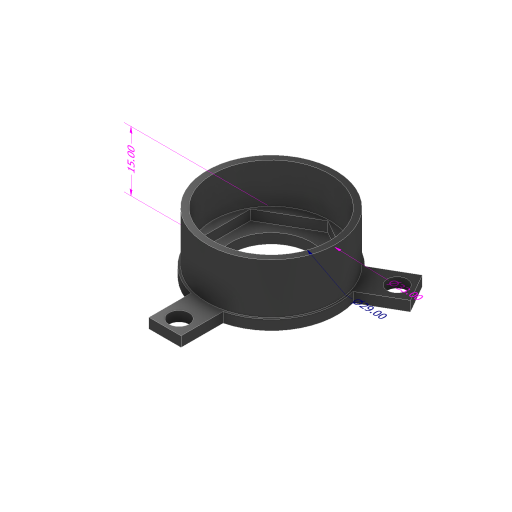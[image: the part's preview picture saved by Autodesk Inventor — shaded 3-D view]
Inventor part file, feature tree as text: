
AUTODESK INVENTOR PART (.ipt)
format: ipt  version: 2024 (Build 280153000, 153)  size: 205,824 bytes
history: native  units: mm
features: extrude x6, other x4, sketch x2
ambient origin geometry x8: Origin, YZ Plane, XZ Plane, XY Plane, X Axis, Y Axis, Z Axis, Center Point
bodies: Solid1 (feature_tree)
feature tree (12):
  other  "Annotations"
  extrude  "Extrusion1"  Depth=33.0mm
  extrude  "Extrusion2"  Depth=2.5mm TaperAngle=0.0deg
  extrude  "Extrusion3"  Depth=15.0mm
  extrude  "Extrusion4"  Depth=2.5mm TaperAngle=0.0deg
  extrude  "Extrusion5"  Depth=15.0mm
  extrude  "Extrusion6"  Depth=10.0mm TaperAngle=0.0deg
  sketch  "Sketch1"  dims[d0=12.25mm d1=33.0mm]
  sketch  "Sketch6"  dims[d2=5.0mm d3=0.0mm d4=2.5mm d5=0.0mm d6=20.0mm d7=2.5mm d8=0.0mm d9=29.0mm d10=10.0mm d11=0.0mm d12=120.0deg d13=120.0deg d14=4.0mm d15=12.0mm d16=8.0mm d17=4.0mm d18=6.5mm d19=5.0mm d20=30.0mm d22=360.0deg d24=2.5mm d25=0.0mm d31=32.0mm d32=0.0mm d33=0.0mm d26=28.118715mm d27=29.0mm d28=31.029943mm d29=33.0mm d30=15.0mm]
  other  "Diameter Dimension 1"
  other  "Diameter Dimension 2"
  other  "Linear Dimension 1"
